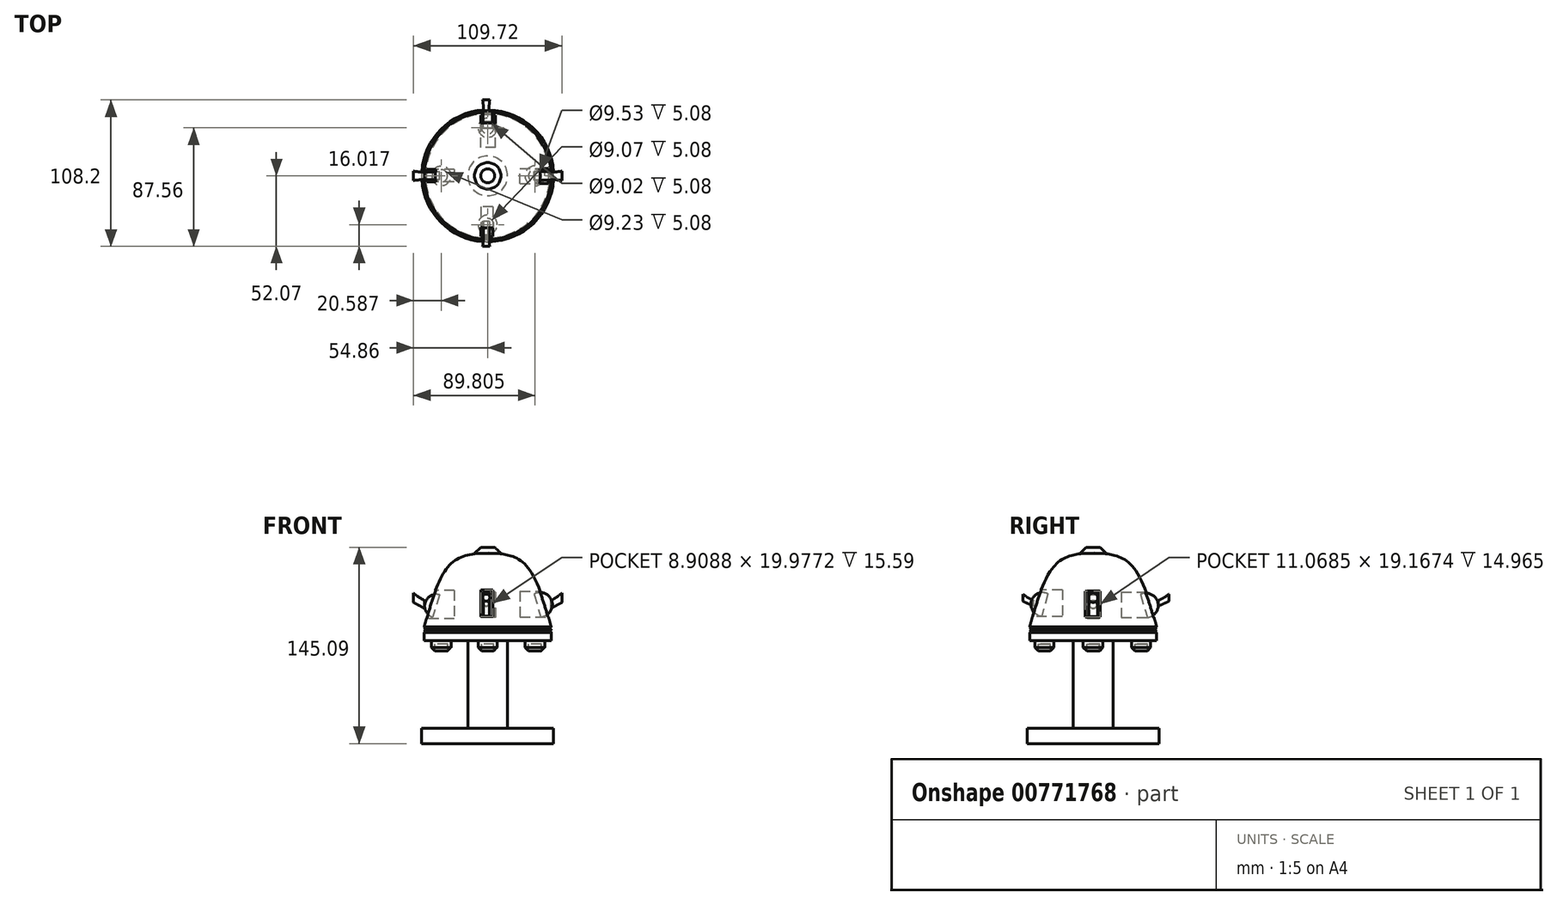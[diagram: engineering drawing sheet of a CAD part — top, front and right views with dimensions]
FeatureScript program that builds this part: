
annotation { "Feature Type Name" : "Feature", "Feature Type Description" : "" }
export const myFeature = defineFeature(function(context is Context, id is Id, definition is map)
    precondition{}
    {
        {
            var Q0;
            Q0=qCreatedBy(makeId("Front.planeOp"),FACE);
            var sketch = newSketch(context, id + "F0", { "sketchPlane" : qUnion([Q0])});
            skLineSegment(sketch, "E0", {"start": v(0, 53.19) * mm, "end": v(0, -53.67) * mm});
            skLineSegment(sketch, "E1", {"start": v(-46.96, -41.02) * mm, "end": v(-46.96, -39.5) * mm});
            skLineSegment(sketch, "E2", {"start": v(-46.96, 0) * mm, "end": v(-46.96, 10.12) * mm});
            skFitSpline(sketch, "E3", {"points": [v(-46.96, 10.12) * mm, v(-26.34, 57.46) * mm, v(0, 64.89) * mm], "startDerivative": vector(27.85, 100.38) * mm, "endDerivative": vector(68.18, 4.1) * mm});
            skLineSegment(sketch, "E4", {"start": v(0, 64.89) * mm, "end": v(0, 53.19) * mm});
            skLineSegment(sketch, "E5", {"start": v(-46.96, 0) * mm, "end": v(-14.7, 0) * mm});
            skLineSegment(sketch, "E6", {"start": v(-14.7, 0) * mm, "end": v(-14.7, -41.02) * mm});
            skLineSegment(sketch, "E7", {"start": v(-46.96, 10.12) * mm, "end": v(-45.93, 9.09) * mm});
            skLineSegment(sketch, "E8", {"start": v(-45.93, 9.09) * mm, "end": v(-46.96, 8.06) * mm});
            skLineSegment(sketch, "E9", {"start": v(-46.96, 8.06) * mm, "end": v(-45.93, 7.03) * mm});
            skLineSegment(sketch, "E10", {"start": v(-45.93, 7.03) * mm, "end": v(-46.96, 6) * mm});
            skLineSegment(sketch, "E11", {"start": v(-14.7, -41.02) * mm, "end": v(-14.7, -64.92) * mm});
            skLineSegment(sketch, "E12", {"start": v(-14.7, -64.92) * mm, "end": v(-48.74, -64.92) * mm});
            skLineSegment(sketch, "E13", {"start": v(-48.74, -64.92) * mm, "end": v(-48.74, -76.26) * mm});
            skLineSegment(sketch, "E14", {"start": v(-48.74, -76.26) * mm, "end": v(0, -76.26) * mm});
            skLineSegment(sketch, "E15", {"start": v(0, -76.26) * mm, "end": v(0, -8.2) * mm});
            skPoint(sketch, "E16.end.orphan", {"position": v(-46.96, -41.02) * mm});
            skSolve(sketch);
        }
        {
            var Q0;
            Q0=makeQuery(id+"F0.imprint","IMPRINT",FACE,{"disambiguationData":[TD([[makeQuery(id+"F0.imprint","IMPRINT",EDGE,{"derivedFrom":sQuery(id+"F0.wireOp",EDGE,"E0")}),-1.0]])]});
            var Q1;
            Q1=sQuery(id+"F0.wireOp",EDGE,"E0");
            revolve(context, id + "F1", {"entities" : qUnion([Q0]), "axis" : qUnion([Q1]), "revolveType" : RevolveType.FULL});
        }
        {
            var Q0;
            Q0=qCreatedBy(makeId("Front.planeOp"),FACE);
            cPlane(context, id + "F2", {"entities" : qUnion([Q0]), "cplaneType" : CPlaneType.OFFSET, "offset" : 48.26 * mm, "width" : 152.4 * mm, "height" : 152.4 * mm});
        }
        {
            var Q0;
            Q0=qCreatedBy(id+"F2.planeOp",FACE);
            var sketch = newSketch(context, id + "F3", { "sketchPlane" : qUnion([Q0])});
            skLineSegment(sketch, "E17.bottom", {"start": v(3.91, 37.5) * mm, "end": v(-5, 37.5) * mm});
            skLineSegment(sketch, "E17.top", {"start": v(3.91, 17.52) * mm, "end": v(-5, 17.52) * mm});
            skLineSegment(sketch, "E17.left", {"start": v(3.91, 37.5) * mm, "end": v(3.91, 17.52) * mm});
            skLineSegment(sketch, "E17.right", {"start": v(-5, 37.5) * mm, "end": v(-5, 17.52) * mm});
            skSolve(sketch);
        }
        {
            var Q0;
            Q0=qSketchRegion(id+"F3",true);
            extrude(context, id + "F4", {"entities" : qUnion([Q0]), "operationType" : NewBodyOperationType.REMOVE, "oppositeDirection" : true, "depth" : 25.4 * mm, "offsetDistance" : 25.4 * mm});
        }
        {
            var Q0;
            Q0=qCreatedBy(makeId("Right.planeOp"),FACE);
            cPlane(context, id + "F5", {"entities" : qUnion([Q0]), "cplaneType" : CPlaneType.OFFSET, "offset" : 1.02 * mm, "oppositeDirection" : true, "width" : 152.4 * mm, "height" : 152.4 * mm});
        }
        {
            var Q0;
            Q0=qCreatedBy(id+"F5.planeOp",FACE);
            var sketch = newSketch(context, id + "F6", { "sketchPlane" : qUnion([Q0])});
            skLineSegment(sketch, "E18", {"start": v(-33.61, 34.52) * mm, "end": v(-37.93, 18.06) * mm});
            skArc(sketch, "E19", {"start": v(-33.61, 34.52) * mm, "mid": v(-45.75, 28.9) * mm, "end": v(-37.93, 18.06) * mm});
            skSolve(sketch);
        }
        {
            var Q0;
            Q0=qSketchRegion(id+"F6",true);
            extrude(context, id + "F7", {"entities" : qUnion([Q0]), "endBound" : BoundingType.SYMMETRIC, "depth" : 4.57 * mm, "offsetDistance" : 25.4 * mm});
        }
        {
            var Q0;
            Q0=qCreatedBy(id+"F5.planeOp",FACE);
            cPlane(context, id + "F8", {"entities" : qUnion([Q0]), "cplaneType" : CPlaneType.OFFSET, "offset" : 45.97 * mm, "oppositeDirection" : true, "width" : 152.4 * mm, "height" : 152.4 * mm});
        }
        {
            var Q0;
            Q0=qCreatedBy(id+"F8.planeOp",FACE);
            var sketch = newSketch(context, id + "F9", { "sketchPlane" : qUnion([Q0])});
            skLineSegment(sketch, "E20.bottom", {"start": v(4.72, 36.95) * mm, "end": v(-4.45, 36.95) * mm});
            skLineSegment(sketch, "E20.top", {"start": v(4.72, 16.17) * mm, "end": v(-4.45, 16.17) * mm});
            skLineSegment(sketch, "E20.left", {"start": v(4.72, 36.95) * mm, "end": v(4.72, 16.17) * mm});
            skLineSegment(sketch, "E20.right", {"start": v(-4.45, 36.95) * mm, "end": v(-4.45, 16.17) * mm});
            skSolve(sketch);
        }
        {
            var Q0;
            Q0=qSketchRegion(id+"F9",true);
            extrude(context, id + "F10", {"entities" : qUnion([Q0]), "operationType" : NewBodyOperationType.REMOVE, "depth" : 22.35 * mm, "offsetDistance" : 25.4 * mm});
        }
        {
            var Q0;
            Q0=qCreatedBy(makeId("Front.planeOp"),FACE);
            var sketch = newSketch(context, id + "F11", { "sketchPlane" : qUnion([Q0])});
            skLineSegment(sketch, "E21", {"start": v(-35.5, 33.71) * mm, "end": v(-40.63, 17.25) * mm});
            skArc(sketch, "E22", {"start": v(-35.5, 33.71) * mm, "mid": v(-46.19, 28) * mm, "end": v(-40.63, 17.25) * mm});
            skSolve(sketch);
        }
        {
            var Q0;
            Q0=qSketchRegion(id+"F11",true);
            extrude(context, id + "F12", {"entities" : qUnion([Q0]), "endBound" : BoundingType.SYMMETRIC, "depth" : 5.6 * mm, "offsetDistance" : 25.4 * mm});
        }
        {
            var Q0;
            Q0=qCreatedBy(id+"F8.planeOp",FACE);
            cPlane(context, id + "F13", {"entities" : qUnion([Q0]), "cplaneType" : CPlaneType.OFFSET, "offset" : 96.27 * mm, "width" : 152.4 * mm, "height" : 152.4 * mm});
        }
        {
            var Q0;
            Q0=qCreatedBy(id+"F13.planeOp",FACE);
            var sketch = newSketch(context, id + "F14", { "sketchPlane" : qUnion([Q0])});
            skLineSegment(sketch, "E23.bottom", {"start": v(-5.8, 36.41) * mm, "end": v(5.26, 36.41) * mm});
            skLineSegment(sketch, "E23.top", {"start": v(-5.8, 17.25) * mm, "end": v(5.26, 17.25) * mm});
            skLineSegment(sketch, "E23.left", {"start": v(-5.8, 36.41) * mm, "end": v(-5.8, 17.25) * mm});
            skLineSegment(sketch, "E23.right", {"start": v(5.26, 36.41) * mm, "end": v(5.26, 17.25) * mm});
            skSolve(sketch);
        }
        {
            var Q0;
            Q0=qSketchRegion(id+"F14",true);
            extrude(context, id + "F15", {"entities" : qUnion([Q0]), "operationType" : NewBodyOperationType.REMOVE, "oppositeDirection" : true, "depth" : 25.4 * mm, "offsetDistance" : 25.4 * mm});
        }
        {
            var Q0;
            Q0=qCreatedBy(makeId("Front.planeOp"),FACE);
            var sketch = newSketch(context, id + "F16", { "sketchPlane" : qUnion([Q0])});
            skLineSegment(sketch, "E24", {"start": v(34.42, 34.25) * mm, "end": v(39, 17.52) * mm});
            skArc(sketch, "E25", {"start": v(39, 17.52) * mm, "mid": v(47.5, 28.84) * mm, "end": v(34.42, 34.25) * mm});
            skSolve(sketch);
        }
        {
            var Q0;
            Q0=qSketchRegion(id+"F16",true);
            extrude(context, id + "F17", {"entities" : qUnion([Q0]), "endBound" : BoundingType.SYMMETRIC, "depth" : 6.6 * mm, "offsetDistance" : 25.4 * mm});
        }
        {
            var Q0;
            Q0=qCreatedBy(makeId("Front.planeOp"),FACE);
            cPlane(context, id + "F18", {"entities" : qUnion([Q0]), "cplaneType" : CPlaneType.OFFSET, "offset" : 49.78 * mm, "oppositeDirection" : true, "width" : 152.4 * mm, "height" : 152.4 * mm});
        }
        {
            var Q0;
            Q0=qCreatedBy(id+"F18.planeOp",FACE);
            var sketch = newSketch(context, id + "F19", { "sketchPlane" : qUnion([Q0])});
            skLineSegment(sketch, "E26.bottom", {"start": v(5.8, 35.6) * mm, "end": v(-5, 35.6) * mm});
            skLineSegment(sketch, "E26.top", {"start": v(5.8, 16.98) * mm, "end": v(-5, 16.98) * mm});
            skLineSegment(sketch, "E26.left", {"start": v(5.8, 35.6) * mm, "end": v(5.8, 16.98) * mm});
            skLineSegment(sketch, "E26.right", {"start": v(-5, 35.6) * mm, "end": v(-5, 16.98) * mm});
            skSolve(sketch);
        }
        {
            var Q0;
            Q0=qSketchRegion(id+"F19",true);
            extrude(context, id + "F20", {"entities" : qUnion([Q0]), "operationType" : NewBodyOperationType.REMOVE, "depth" : 28.96 * mm, "offsetDistance" : 25.4 * mm});
        }
        {
            var Q0;
            Q0=qCreatedBy(makeId("Right.planeOp"),FACE);
            var sketch = newSketch(context, id + "F21", { "sketchPlane" : qUnion([Q0])});
            skLineSegment(sketch, "E27", {"start": v(34.94, 33.98) * mm, "end": v(40.07, 16.98) * mm});
            skArc(sketch, "E28", {"start": v(40.07, 16.98) * mm, "mid": v(47.7, 28.55) * mm, "end": v(34.94, 33.98) * mm});
            skSolve(sketch);
        }
        {
            var Q0;
            Q0=qSketchRegion(id+"F21",true);
            extrude(context, id + "F22", {"entities" : qUnion([Q0]), "endBound" : BoundingType.SYMMETRIC, "depth" : 7.11 * mm, "offsetDistance" : 25.4 * mm});
        }
        {
            var Q0;
            Q0=qCreatedBy(makeId("Top.planeOp"),FACE);
            var sketch = newSketch(context, id + "F23", { "sketchPlane" : qUnion([Q0])});
            skCircle(sketch, "E29", {"center": v(-34.27, 0) * mm, "radius": 7.15 * mm});
            skSolve(sketch);
        }
        {
            var Q0;
            Q0=qSketchRegion(id+"F23",true);
            extrude(context, id + "F24", {"entities" : qUnion([Q0]), "oppositeDirection" : true, "depth" : 10.16 * mm, "offsetDistance" : 25.4 * mm});
        }
        {
            var Q0;
            Q0=makeQuery(id+"F24.opExtrude","CAP_FACE",FACE,{"disambiguationData":[OSD([sQuery(id+"F23.wireOp",EDGE,"E29")])],"isStart":false});
            shell(context, id + "F25", {"entities" : qUnion([Q0]), "thickness" : 2.54 * mm});
        }
        {
            var Q0;
            Q0=makeQuery(id+"F24.opExtrude","CAP_EDGE",EDGE,{"disambiguationData":[OSD([sQuery(id+"F23.wireOp",EDGE,"E29")])],"isStart":false});
            chamfer(context, id + "F26", {"entities" : qUnion([Q0]), "width" : 5.08 * mm, "tangentPropagation" : true});
        }
        {
            var Q0;
            Q0=qCreatedBy(makeId("Top.planeOp"),FACE);
            var sketch = newSketch(context, id + "F27", { "sketchPlane" : qUnion([Q0])});
            skCircle(sketch, "E30", {"center": v(34.95, 0) * mm, "radius": 7.3 * mm});
            skSolve(sketch);
        }
        {
            var Q0;
            Q0=qSketchRegion(id+"F27",true);
            extrude(context, id + "F28", {"entities" : qUnion([Q0]), "oppositeDirection" : true, "depth" : 10.16 * mm, "offsetDistance" : 25.4 * mm});
        }
        {
            var Q0;
            Q0=makeQuery(id+"F28.opExtrude","CAP_FACE",FACE,{"disambiguationData":[OSD([sQuery(id+"F27.wireOp",EDGE,"E30")])],"isStart":false});
            shell(context, id + "F29", {"entities" : qUnion([Q0]), "thickness" : 2.54 * mm});
        }
        {
            var Q0;
            Q0=makeQuery(id+"F28.opExtrude","CAP_EDGE",EDGE,{"disambiguationData":[OSD([sQuery(id+"F27.wireOp",EDGE,"E30")])],"isStart":false});
            chamfer(context, id + "F30", {"entities" : qUnion([Q0]), "width" : 5.08 * mm, "tangentPropagation" : true});
        }
        {
            var Q0;
            Q0=qCreatedBy(makeId("Top.planeOp"),FACE);
            var sketch = newSketch(context, id + "F31", { "sketchPlane" : qUnion([Q0])});
            skCircle(sketch, "E31", {"center": v(0, 35.5) * mm, "radius": 7.05 * mm});
            skSolve(sketch);
        }
        {
            var Q0;
            Q0=qSketchRegion(id+"F31",true);
            extrude(context, id + "F32", {"entities" : qUnion([Q0]), "oppositeDirection" : true, "depth" : 10.16 * mm, "offsetDistance" : 25.4 * mm});
        }
        {
            var Q0;
            Q0=makeQuery(id+"F32.opExtrude","CAP_FACE",FACE,{"disambiguationData":[OSD([sQuery(id+"F31.wireOp",EDGE,"E31")])],"isStart":false});
            shell(context, id + "F33", {"entities" : qUnion([Q0]), "thickness" : 2.54 * mm});
        }
        {
            var Q0;
            Q0=makeQuery(id+"F32.opExtrude","CAP_EDGE",EDGE,{"disambiguationData":[OSD([sQuery(id+"F31.wireOp",EDGE,"E31")])],"isStart":false});
            chamfer(context, id + "F34", {"entities" : qUnion([Q0]), "width" : 5.08 * mm, "tangentPropagation" : true});
        }
        {
            var Q0;
            Q0=qCreatedBy(makeId("Top.planeOp"),FACE);
            var sketch = newSketch(context, id + "F35", { "sketchPlane" : qUnion([Q0])});
            skCircle(sketch, "E32", {"center": v(0, -36.05) * mm, "radius": 7.07 * mm});
            skSolve(sketch);
        }
        {
            var Q0;
            Q0=qSketchRegion(id+"F35",true);
            extrude(context, id + "F36", {"entities" : qUnion([Q0]), "oppositeDirection" : true, "depth" : 10.16 * mm, "offsetDistance" : 25.4 * mm});
        }
        {
            var Q0;
            Q0=makeQuery(id+"F36.opExtrude","CAP_FACE",FACE,{"disambiguationData":[OSD([sQuery(id+"F35.wireOp",EDGE,"E32")])],"isStart":false});
            shell(context, id + "F37", {"entities" : qUnion([Q0]), "thickness" : 2.54 * mm});
        }
        {
            var Q0;
            Q0=makeQuery(id+"F36.opExtrude","CAP_EDGE",EDGE,{"disambiguationData":[OSD([sQuery(id+"F35.wireOp",EDGE,"E32")])],"isStart":false});
            chamfer(context, id + "F38", {"entities" : qUnion([Q0]), "width" : 5.08 * mm, "tangentPropagation" : true});
        }
        {
            var Q0;
            Q0=qCreatedBy(makeId("Top.planeOp"),FACE);
            cPlane(context, id + "F39", {"entities" : qUnion([Q0]), "cplaneType" : CPlaneType.OFFSET, "offset" : 64.26 * mm, "width" : 152.4 * mm, "height" : 152.4 * mm});
        }
        {
            var Q0;
            Q0=qCreatedBy(id+"F39.planeOp",FACE);
            var sketch = newSketch(context, id + "F40", { "sketchPlane" : qUnion([Q0])});
            skCircle(sketch, "E33", {"center": v(0, 0) * mm, "radius": 10.3 * mm});
            skSolve(sketch);
        }
        {
            var Q0;
            Q0=qSketchRegion(id+"F40",true);
            extrude(context, id + "F41", {"entities" : qUnion([Q0]), "depth" : 4.57 * mm, "offsetDistance" : 25.4 * mm});
        }
        {
            var Q0;
            Q0=makeQuery(id+"F41.opExtrude","CAP_EDGE",EDGE,{"disambiguationData":[OSD([sQuery(id+"F40.wireOp",EDGE,"E33")])],"isStart":false});
            chamfer(context, id + "F42", {"entities" : qUnion([Q0]), "width" : 5.08 * mm, "tangentPropagation" : true});
        }
        {
            var Q0;
            Q0=qCreatedBy(id+"F2.planeOp",FACE);
            cPlane(context, id + "F43", {"entities" : qUnion([Q0]), "cplaneType" : CPlaneType.OFFSET, "offset" : 4.32 * mm, "oppositeDirection" : true, "width" : 152.4 * mm, "height" : 152.4 * mm});
        }
        {
            var Q0;
            Q0=qCreatedBy(id+"F2.planeOp",FACE);
            cPlane(context, id + "F44", {"entities" : qUnion([Q0]), "cplaneType" : CPlaneType.OFFSET, "offset" : 3.8 * mm, "width" : 152.4 * mm, "height" : 152.4 * mm});
        }
        {
            var Q0;
            Q0=qCreatedBy(id+"F43.planeOp",FACE);
            var sketch = newSketch(context, id + "F45", { "sketchPlane" : qUnion([Q0])});
            skCircle(sketch, "E34", {"center": v(-1.1, 27.43) * mm, "radius": 2.09 * mm});
            skSolve(sketch);
        }
        {
            var Q0;
            Q0=qCreatedBy(id+"F2.planeOp",FACE);
            var sketch = newSketch(context, id + "F46", { "sketchPlane" : qUnion([Q0])});
            skCircle(sketch, "E35", {"center": v(-1.1, 29.49) * mm, "radius": 2.2 * mm});
            skSolve(sketch);
        }
        {
            var Q0;
            Q0=qCreatedBy(id+"F44.planeOp",FACE);
            var sketch = newSketch(context, id + "F47", { "sketchPlane" : qUnion([Q0])});
            skCircle(sketch, "E36", {"center": v(-1.1, 31.68) * mm, "radius": 2.63 * mm});
            skSolve(sketch);
        }
        {
            var Q1;
            Q1=qSketchRegion(id+"F45",true);
            var Q2;
            Q2=qSketchRegion(id+"F46",true);
            var Q3;
            Q3=qSketchRegion(id+"F47",true);
            loft(context, id + "F48", {"sheetProfilesArray" : [{ "sheetProfileEntities" : qUnion([Q1]) }, { "sheetProfileEntities" : qUnion([Q2]) }, { "sheetProfileEntities" : qUnion([Q3]) }]});
        }
        {
            var Q0;
            Q0=qCreatedBy(makeId("Front.planeOp"),FACE);
            cPlane(context, id + "F49", {"entities" : qUnion([Q0]), "cplaneType" : CPlaneType.OFFSET, "offset" : 2.03 * mm, "oppositeDirection" : true, "width" : 152.4 * mm, "height" : 152.4 * mm});
        }
        {
            var Q0;
            Q0=makeQuery(id+"F48.opLoft","SWEPT_BODY",BODY,{"disambiguationData":[OSD([makeQuery(id+"F45.imprint","IMPRINT",FACE,{"disambiguationData":[TD([[makeQuery(id+"F45.imprint","IMPRINT",EDGE,{"derivedFrom":sQuery(id+"F45.wireOp",EDGE,"E34")}),1.0]])]}),sQuery(id+"F46.wireOp",EDGE,"E35"),makeQuery(id+"F47.imprint","IMPRINT",FACE,{"disambiguationData":[TD([[makeQuery(id+"F47.imprint","IMPRINT",EDGE,{"derivedFrom":sQuery(id+"F47.wireOp",EDGE,"E36")}),1.0]])]})])]});
            var Q1;
            Q1=qCreatedBy(id+"F49.planeOp",FACE);
            mirror(context, id + "F50", {"entities" : qUnion([Q0]), "mirrorPlane" : qUnion([Q1])});
        }
        {
            var Q0;
            Q0=qCreatedBy(makeId("Right.planeOp"),FACE);
            cPlane(context, id + "F51", {"entities" : qUnion([Q0]), "cplaneType" : CPlaneType.OFFSET, "offset" : 46.74 * mm, "width" : 152.4 * mm, "height" : 152.4 * mm});
        }
        {
            var Q0;
            Q0=qCreatedBy(id+"F51.planeOp",FACE);
            cPlane(context, id + "F52", {"entities" : qUnion([Q0]), "cplaneType" : CPlaneType.OFFSET, "offset" : 4.57 * mm, "width" : 152.4 * mm, "height" : 152.4 * mm});
        }
        {
            var Q0;
            Q0=qCreatedBy(id+"F52.planeOp",FACE);
            cPlane(context, id + "F53", {"entities" : qUnion([Q0]), "cplaneType" : CPlaneType.OFFSET, "offset" : 3.56 * mm, "width" : 152.4 * mm, "height" : 152.4 * mm});
        }
        {
            var Q0;
            Q0=qCreatedBy(id+"F51.planeOp",FACE);
            var sketch = newSketch(context, id + "F54", { "sketchPlane" : qUnion([Q0])});
            skCircle(sketch, "E37", {"center": v(0, 26.61) * mm, "radius": 2.94 * mm});
            skSolve(sketch);
        }
        {
            var Q0;
            Q0=qCreatedBy(id+"F52.planeOp",FACE);
            var sketch = newSketch(context, id + "F55", { "sketchPlane" : qUnion([Q0])});
            skCircle(sketch, "E38", {"center": v(0, 29.29) * mm, "radius": 3.02 * mm});
            skSolve(sketch);
        }
        {
            var Q0;
            Q0=qCreatedBy(id+"F53.planeOp",FACE);
            var sketch = newSketch(context, id + "F56", { "sketchPlane" : qUnion([Q0])});
            skCircle(sketch, "E39", {"center": v(0, 31.58) * mm, "radius": 3.44 * mm});
            skSolve(sketch);
        }
        {
            var Q1;
            Q1=qSketchRegion(id+"F54",true);
            var Q2;
            Q2=qSketchRegion(id+"F55",true);
            var Q3;
            Q3=qSketchRegion(id+"F56",true);
            loft(context, id + "F57", {"sheetProfilesArray" : [{ "sheetProfileEntities" : qUnion([Q1]) }, { "sheetProfileEntities" : qUnion([Q2]) }, { "sheetProfileEntities" : qUnion([Q3]) }]});
        }
        {
            var Q0;
            Q0=qCreatedBy(id+"F52.planeOp",FACE);
            cPlane(context, id + "F58", {"entities" : qUnion([Q0]), "cplaneType" : CPlaneType.OFFSET, "offset" : 51.3 * mm, "oppositeDirection" : true, "width" : 152.4 * mm, "height" : 152.4 * mm});
        }
        {
            var Q0;
            Q0=makeQuery(id+"F57.opLoft","SWEPT_BODY",BODY,{"disambiguationData":[OSD([makeQuery(id+"F54.imprint","IMPRINT",FACE,{"disambiguationData":[TD([[makeQuery(id+"F54.imprint","IMPRINT",EDGE,{"derivedFrom":sQuery(id+"F54.wireOp",EDGE,"E37")}),1.0]])]}),sQuery(id+"F55.wireOp",EDGE,"E38"),makeQuery(id+"F56.imprint","IMPRINT",FACE,{"disambiguationData":[TD([[makeQuery(id+"F56.imprint","IMPRINT",EDGE,{"derivedFrom":sQuery(id+"F56.wireOp",EDGE,"E39")}),1.0]])]})])]});
            var Q1;
            Q1=qCreatedBy(id+"F58.planeOp",FACE);
            mirror(context, id + "F59", {"entities" : qUnion([Q0]), "mirrorPlane" : qUnion([Q1])});
        }
    });
